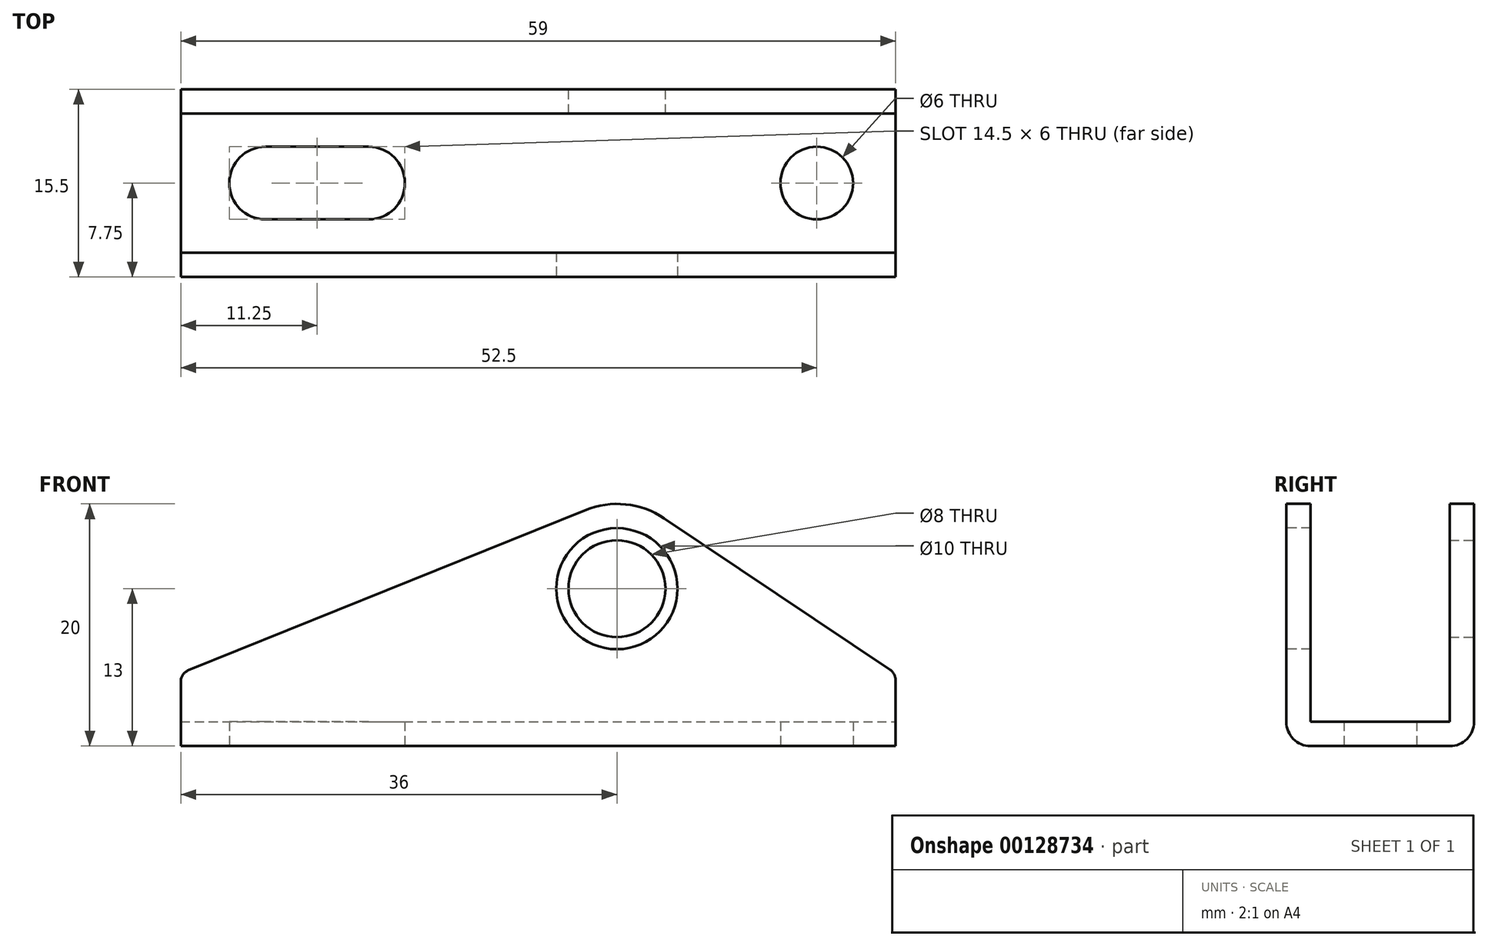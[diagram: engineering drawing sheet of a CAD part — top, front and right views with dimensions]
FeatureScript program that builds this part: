
annotation { "Feature Type Name" : "Feature", "Feature Type Description" : "" }
export const myFeature = defineFeature(function(context is Context, id is Id, definition is map)
    precondition{}
    {
        {
            var Q0;
            Q0=qCreatedBy(makeId("Front.planeOp"),FACE);
            var sketch = newSketch(context, id + "F0", { "sketchPlane" : qUnion([Q0])});
            skCircle(sketch, "E0.0", {"center": v(0, 0) * mm, "radius": 7 * mm});
            skLineSegment(sketch, "E1", {"start": v(-2.62, 6.49) * mm, "end": v(-36, -7) * mm});
            skLineSegment(sketch, "E2", {"start": v(3.9, 5.81) * mm, "end": v(23, -7) * mm});
            skLineSegment(sketch, "E3.bottom", {"start": v(23, -7) * mm, "end": v(-36, -7) * mm});
            skLineSegment(sketch, "E3.top", {"start": v(23, -13) * mm, "end": v(-36, -13) * mm});
            skLineSegment(sketch, "E3.left", {"start": v(23, -7) * mm, "end": v(23, -13) * mm});
            skLineSegment(sketch, "E3.right", {"start": v(-36, -7) * mm, "end": v(-36, -13) * mm});
            skLineSegment(sketch, "E4", {"start": v(0, 0) * mm, "end": v(0, -7) * mm, "construction": true});
            skPoint(sketch, "E5", {"position": v(0, 7) * mm});
            skCircle(sketch, "E6", {"center": v(0, 0) * mm, "radius": 5 * mm});
            skCircle(sketch, "E7", {"center": v(0, 0) * mm, "radius": 4 * mm});
            skSolve(sketch);
        }
        {
            var Q0;
            {var subQ0=sQuery(id+"F0.wireOp",EDGE,"E1");Q0=makeQuery(id+"F0.imprint","IMPRINT",FACE,{"disambiguationData":[TD([[makeQuery(id+"F0.imprint","IMPRINT",EDGE,{"derivedFrom":subQ0}),1.0]])]});}
            var Q1;
            Q1=makeQuery(id+"F0.imprint","IMPRINT",FACE,{"disambiguationData":[TD([[makeQuery(id+"F0.imprint","IMPRINT",EDGE,{"derivedFrom":sQuery(id+"F0.wireOp",EDGE,"1n37zXkw-yRvc-RGLe-vBZi-SAm0DfBKIiOk")}),-1.0]])]});
            var Q2;
            Q2=makeQuery(id+"F0.imprint","IMPRINT",FACE,{"disambiguationData":[TD([[makeQuery(id+"F0.imprint","IMPRINT",EDGE,{"derivedFrom":sQuery(id+"F0.wireOp",EDGE,"1n37zXkw-yRvc-RGLe-vBZi-SAm0DfBKIiOk")}),1.0]])]});
            var Q3;
            Q3=makeQuery(id+"F0.imprint","IMPRINT",FACE,{"disambiguationData":[TD([[makeQuery(id+"F0.imprint","IMPRINT",EDGE,{"derivedFrom":sQuery(id+"F0.wireOp",EDGE,"E3.bottom")}),1.0]])]});
            var Q4;
            {var subQ0=sQuery(id+"F0.wireOp",EDGE,"E2");Q4=makeQuery(id+"F0.imprint","IMPRINT",FACE,{"disambiguationData":[TD([[makeQuery(id+"F0.imprint","IMPRINT",EDGE,{"derivedFrom":subQ0}),-1.0]])]});}
            var Q5;
            Q5=makeQuery(id+"F0.imprint","IMPRINT",FACE,{"disambiguationData":[TD([[makeQuery(id+"F0.imprint","IMPRINT",EDGE,{"derivedFrom":sQuery(id+"F0.wireOp",EDGE,"E6")}),-1.0]])]});
            var Q6;
            Q6=makeQuery(id+"F0.imprint","IMPRINT",FACE,{"disambiguationData":[TD([[makeQuery(id+"F0.imprint","IMPRINT",EDGE,{"derivedFrom":sQuery(id+"F0.wireOp",EDGE,"E6")}),1.0]])]});
            extrude(context, id + "F1", {"entities" : qUnion([Q0, Q1, Q2, Q3, Q4, Q5, Q6]), "depth" : 15.5 * mm});
        }
        {
            var Q0;
            Q0=makeQuery(id+"F1.opExtrude","SWEPT_FACE",FACE,{"disambiguationData":[OSD([sQuery(id+"F0.wireOp",EDGE,"E3.left")])]});
            var sketch = newSketch(context, id + "F2", { "sketchPlane" : qUnion([Q0])});
            skLineSegment(sketch, "E8.bottom", {"start": v(-2, 19.25) * mm, "end": v(-13.5, 19.25) * mm});
            skLineSegment(sketch, "E8.top", {"start": v(-2, -11) * mm, "end": v(-13.5, -11) * mm});
            skLineSegment(sketch, "E8.left", {"start": v(-2, 19.25) * mm, "end": v(-2, -11) * mm});
            skLineSegment(sketch, "E8.right", {"start": v(-13.5, 19.25) * mm, "end": v(-13.5, -11) * mm});
            skPoint(sketch, "E8.middle", {"position": v(-7.75, 4.12) * mm});
            skPoint(sketch, "E8.middle.positionSnap0", {"position": v(-7.75, -13) * mm});
            skPoint(sketch, "E8.centerSnap0", {"position": v(-7.75, -13) * mm});
            skSolve(sketch);
        }
        {
            var Q0;
            {var subQ0=sQuery(id+"F2.wireOp",EDGE,"E8.bottom");Q0=makeQuery(id+"F2.imprint","IMPRINT",FACE,{"disambiguationData":[TD([[makeQuery(id+"F2.imprint","IMPRINT",EDGE,{"derivedFrom":subQ0}),1.0]])]});}
            var Q1;
            {var subQ0=sQuery(id+"F2.wireOp",EDGE,"E8.top");Q1=makeQuery(id+"F2.imprint","IMPRINT",FACE,{"disambiguationData":[TD([[makeQuery(id+"F2.imprint","IMPRINT",EDGE,{"derivedFrom":subQ0}),-1.0]])]});}
            extrude(context, id + "F3", {"entities" : qUnion([Q0, Q1]), "operationType" : NewBodyOperationType.REMOVE, "endBound" : BoundingType.THROUGH_ALL, "oppositeDirection" : true, "depth" : 25 * mm});
        }
        {
            var Q0;
            Q0=makeQuery(id+"F1.opExtrude","SWEPT_FACE",FACE,{"disambiguationData":[OSD([sQuery(id+"F0.wireOp",EDGE,"E3.top")])]});
            var sketch = newSketch(context, id + "F4", { "sketchPlane" : qUnion([Q0])});
            skCircle(sketch, "E9", {"center": v(-29, 7.75) * mm, "radius": 3 * mm});
            skPoint(sketch, "E9.centerSnap0", {"position": v(-36, 7.75) * mm});
            skCircle(sketch, "E10", {"center": v(16.5, 7.75) * mm, "radius": 3 * mm});
            skPoint(sketch, "E10.centerSnap0", {"position": v(23, 7.75) * mm});
            skCircle(sketch, "E11", {"center": v(-20.5, 7.75) * mm, "radius": 3 * mm});
            skLineSegment(sketch, "E12", {"start": v(-20.5, 10.75) * mm, "end": v(-29, 10.75) * mm});
            skLineSegment(sketch, "E13", {"start": v(-29, 4.75) * mm, "end": v(-20.5, 4.75) * mm});
            skSolve(sketch);
        }
        {
            var Q0;
            {var subQ0=sQuery(id+"F4.wireOp",EDGE,"E9");var subQ1=makeQuery(id+"F4.imprint","INTERSECT",VERTEX,{"derivedFrom":[subQ0,sQuery(id+"F4.wireOp",EDGE,"E12")]});Q0=makeQuery(id+"F4.imprint","IMPRINT",FACE,{"disambiguationData":[TD([[makeQuery(id+"F4.imprint","IMPRINT",EDGE,{"disambiguationData":[TD([[subQ1,-1.0]])],"derivedFrom":subQ0}),1.0]])]});}
            var Q1;
            {var subQ0=sQuery(id+"F4.wireOp",EDGE,"E12");Q1=makeQuery(id+"F4.imprint","IMPRINT",FACE,{"disambiguationData":[TD([[makeQuery(id+"F4.imprint","IMPRINT",EDGE,{"derivedFrom":subQ0}),1.0]])]});}
            var Q2;
            {var subQ0=sQuery(id+"F4.wireOp",EDGE,"E11");var subQ1=makeQuery(id+"F4.imprint","INTERSECT",VERTEX,{"derivedFrom":[subQ0,sQuery(id+"F4.wireOp",EDGE,"E12")]});Q2=makeQuery(id+"F4.imprint","IMPRINT",FACE,{"disambiguationData":[TD([[makeQuery(id+"F4.imprint","IMPRINT",EDGE,{"disambiguationData":[TD([[subQ1,-1.0]])],"derivedFrom":subQ0}),1.0]])]});}
            var Q3;
            Q3=makeQuery(id+"F4.imprint","IMPRINT",FACE,{"disambiguationData":[TD([[makeQuery(id+"F4.imprint","IMPRINT",EDGE,{"derivedFrom":sQuery(id+"F4.wireOp",EDGE,"E10")}),1.0]])]});
            extrude(context, id + "F5", {"entities" : qUnion([Q0, Q1, Q2, Q3]), "operationType" : NewBodyOperationType.REMOVE, "oppositeDirection" : true, "depth" : 2 * mm});
        }
        {
            var Q0;
            {var subQ0=sQuery(id+"F0.wireOp",EDGE,"E3.right");var subQ1=sQuery(id+"F0.wireOp",EDGE,"E1");Q0=makeQuery(id+"F3.boolean.opBoolean","SPLIT",EDGE,{"disambiguationData":[TD([makeQuery(id+"F3.opExtrude","SWEPT_FACE",FACE,{"disambiguationData":[OSD([sQuery(id+"F2.wireOp",EDGE,"E8.right")])]})])],"derivedFrom":makeQuery(id+"F1.opExtrude","SWEPT_EDGE",EDGE,{"disambiguationData":[OSD([subQ1,sQuery(id+"F0.wireOp",EDGE,"E3.bottom"),subQ0])]})});}
            var Q1;
            {var subQ0=sQuery(id+"F0.wireOp",EDGE,"E3.right");var subQ1=sQuery(id+"F0.wireOp",EDGE,"E1");Q1=makeQuery(id+"F3.boolean.opBoolean","SPLIT",EDGE,{"disambiguationData":[TD([makeQuery(id+"F3.opExtrude","SWEPT_FACE",FACE,{"disambiguationData":[OSD([sQuery(id+"F2.wireOp",EDGE,"E8.left")])]})])],"derivedFrom":makeQuery(id+"F1.opExtrude","SWEPT_EDGE",EDGE,{"disambiguationData":[OSD([subQ1,sQuery(id+"F0.wireOp",EDGE,"E3.bottom"),subQ0])]})});}
            var Q2;
            {var subQ0=sQuery(id+"F0.wireOp",EDGE,"E3.left");var subQ1=sQuery(id+"F0.wireOp",EDGE,"E2");Q2=makeQuery(id+"F3.boolean.opBoolean","SPLIT",EDGE,{"disambiguationData":[TD([makeQuery(id+"F3.opExtrude","SWEPT_FACE",FACE,{"disambiguationData":[OSD([sQuery(id+"F2.wireOp",EDGE,"E8.right")])]})])],"derivedFrom":makeQuery(id+"F1.opExtrude","SWEPT_EDGE",EDGE,{"disambiguationData":[OSD([subQ1,sQuery(id+"F0.wireOp",EDGE,"E3.bottom"),subQ0])]})});}
            var Q3;
            {var subQ0=sQuery(id+"F0.wireOp",EDGE,"E3.left");var subQ1=sQuery(id+"F0.wireOp",EDGE,"E2");Q3=makeQuery(id+"F3.boolean.opBoolean","SPLIT",EDGE,{"disambiguationData":[TD([makeQuery(id+"F3.opExtrude","SWEPT_FACE",FACE,{"disambiguationData":[OSD([sQuery(id+"F2.wireOp",EDGE,"E8.left")])]})])],"derivedFrom":makeQuery(id+"F1.opExtrude","SWEPT_EDGE",EDGE,{"disambiguationData":[OSD([subQ1,sQuery(id+"F0.wireOp",EDGE,"E3.bottom"),subQ0])]})});}
            fillet(context, id + "F6", {"entities" : qUnion([Q0, Q1, Q2, Q3]), "radius" : 1 * mm, "tangentPropagation" : true, "allowEdgeOverflow" : false});
        }
        {
            var Q0;
            Q0=makeQuery(id+"F1.opExtrude","CAP_EDGE",EDGE,{"disambiguationData":[OSD([sQuery(id+"F0.wireOp",EDGE,"E3.top")])],"isStart":false});
            var Q1;
            Q1=makeQuery(id+"F1.opExtrude","CAP_EDGE",EDGE,{"disambiguationData":[OSD([sQuery(id+"F0.wireOp",EDGE,"E3.top")])],"isStart":true});
            fillet(context, id + "F7", {"entities" : qUnion([Q0, Q1]), "radius" : 2 * mm, "tangentPropagation" : true, "allowEdgeOverflow" : false});
        }
        {
            var Q0;
            Q0=makeQuery(id+"F1.opExtrude","CAP_FACE",FACE,{"disambiguationData":[OSD([sQuery(id+"F0.wireOp",EDGE,"E0.0"),sQuery(id+"F0.wireOp",EDGE,"E1"),sQuery(id+"F0.wireOp",EDGE,"E2"),sQuery(id+"F0.wireOp",EDGE,"E3.top"),sQuery(id+"F0.wireOp",EDGE,"E3.left"),sQuery(id+"F0.wireOp",EDGE,"E3.right")])],"isStart":false});
            var sketch = newSketch(context, id + "F8", { "sketchPlane" : qUnion([Q0])});
            skCircle(sketch, "E14.0", {"center": v(0, 0) * mm, "radius": 5 * mm});
            skSolve(sketch);
        }
        {
            var Q0;
            Q0=makeQuery(id+"F8.imprint","IMPRINT",FACE,{"disambiguationData":[TD([[makeQuery(id+"F8.imprint","IMPRINT",EDGE,{"derivedFrom":sQuery(id+"F8.wireOp",EDGE,"E14.0")}),1.0]])]});
            var Q1;
            Q1=makeQuery(id+"F3.boolean.opBoolean","COPY",FACE,{"derivedFrom":makeQuery(id+"F3.opExtrude","SWEPT_FACE",FACE,{"disambiguationData":[OSD([sQuery(id+"F2.wireOp",EDGE,"E8.right")])]})});
            extrude(context, id + "F9", {"entities" : qUnion([Q0]), "operationType" : NewBodyOperationType.REMOVE, "endBound" : BoundingType.UP_TO_SURFACE, "oppositeDirection" : true, "endBoundEntityFace" : qUnion([Q1]), "depth" : 25 * mm});
        }
    });
